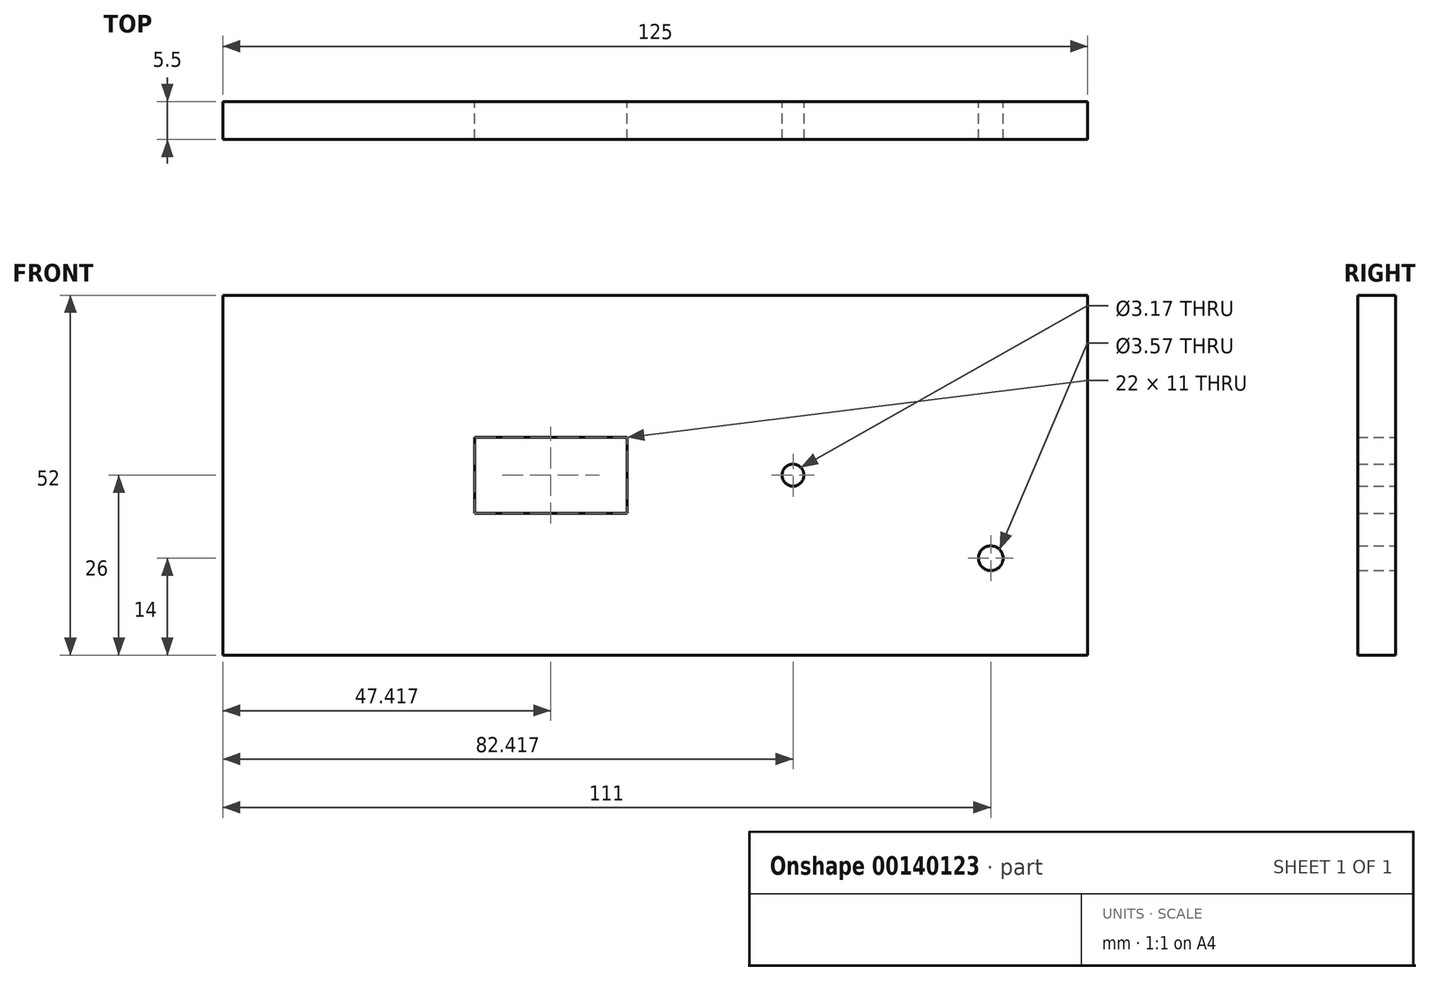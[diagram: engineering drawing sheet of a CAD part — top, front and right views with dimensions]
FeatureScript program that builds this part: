
annotation { "Feature Type Name" : "Feature", "Feature Type Description" : "" }
export const myFeature = defineFeature(function(context is Context, id is Id, definition is map)
    precondition{}
    {
        {
            var Q0;
            Q0=qCreatedBy(makeId("Front.planeOp"),FACE);
            var sketch = newSketch(context, id + "F0", { "sketchPlane" : qUnion([Q0])});
            skLineSegment(sketch, "E0.bottom", {"start": v(0, 0) * mm, "end": v(125, 0) * mm});
            skLineSegment(sketch, "E0.top", {"start": v(0, 52) * mm, "end": v(125, 52) * mm});
            skLineSegment(sketch, "E0.left", {"start": v(0, 0) * mm, "end": v(0, 52) * mm});
            skLineSegment(sketch, "E0.right", {"start": v(125, 0) * mm, "end": v(125, 52) * mm});
            skCircle(sketch, "E1", {"center": v(111, 14) * mm, "radius": 1.79 * mm});
            skCircle(sketch, "E2", {"center": v(82.42, 26) * mm, "radius": 1.59 * mm});
            skLineSegment(sketch, "E3", {"start": v(58.42, 26) * mm, "end": v(58.42, 31.5) * mm});
            skLineSegment(sketch, "E4.bottom", {"start": v(58.42, 31.5) * mm, "end": v(36.42, 31.5) * mm});
            skLineSegment(sketch, "E4.top", {"start": v(58.42, 20.5) * mm, "end": v(36.42, 20.5) * mm});
            skLineSegment(sketch, "E4.left", {"start": v(58.42, 31.5) * mm, "end": v(58.42, 20.5) * mm});
            skLineSegment(sketch, "E4.right", {"start": v(36.42, 31.5) * mm, "end": v(36.42, 20.5) * mm});
            skSolve(sketch);
        }
        {
            var Q0;
            Q0=makeQuery(id+"F0.imprint","IMPRINT",FACE,{"disambiguationData":[TD([[makeQuery(id+"F0.imprint","IMPRINT",EDGE,{"derivedFrom":sQuery(id+"F0.wireOp",EDGE,"E0.bottom")}),1.0]])]});
            extrude(context, id + "F1", {"entities" : qUnion([Q0]), "depth" : 5.5 * mm});
        }
    });
